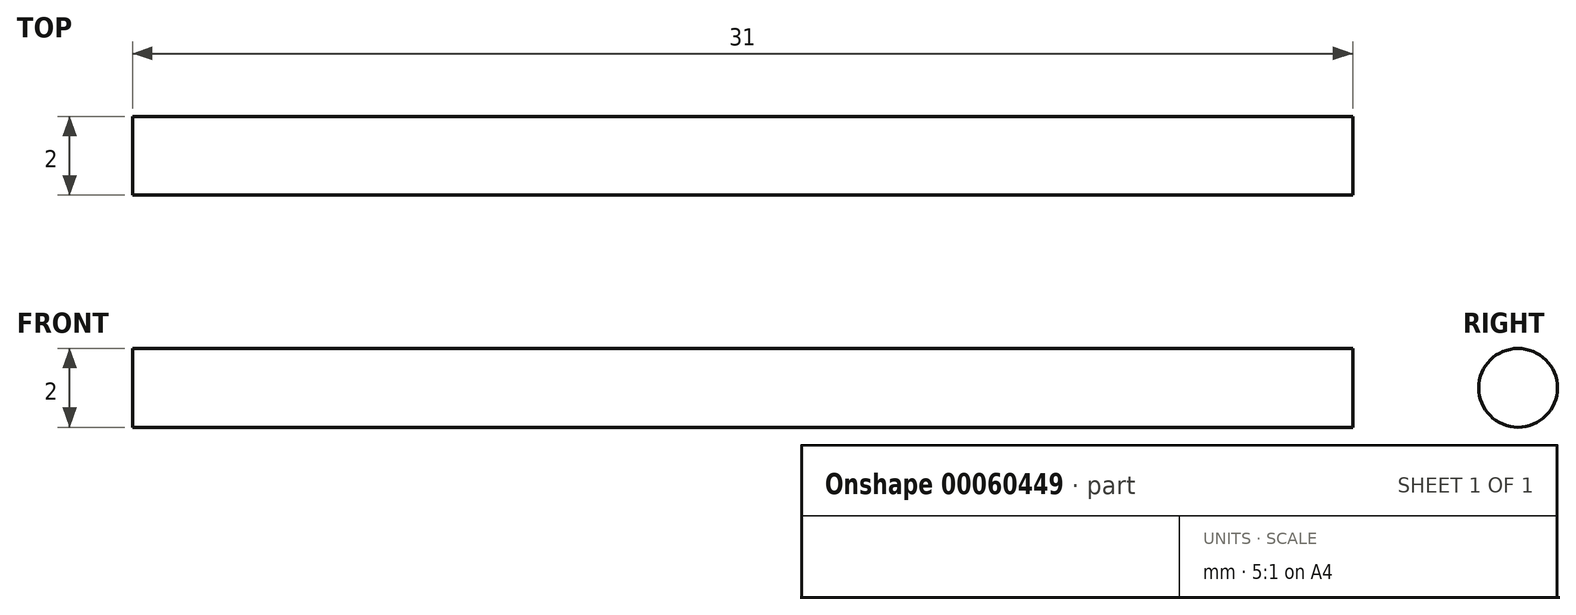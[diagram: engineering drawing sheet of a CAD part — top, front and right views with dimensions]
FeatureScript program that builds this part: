
annotation { "Feature Type Name" : "Feature", "Feature Type Description" : "" }
export const myFeature = defineFeature(function(context is Context, id is Id, definition is map)
    precondition{}
    {
        {
            var Q0;
            Q0=qCreatedBy(makeId("Right.planeOp"),FACE);
            var sketch = newSketch(context, id + "F0", { "sketchPlane" : qUnion([Q0])});
            skCircle(sketch, "E0", {"center": v(0, 0) * mm, "radius": 1 * mm});
            skSolve(sketch);
        }
        {
            var Q0;
            Q0 = qSketchRegion(id + "F0", true);
            extrude(context, id + "F1", {"entities" : qUnion([Q0]), "depth" : 31 * mm});
        }
    });
